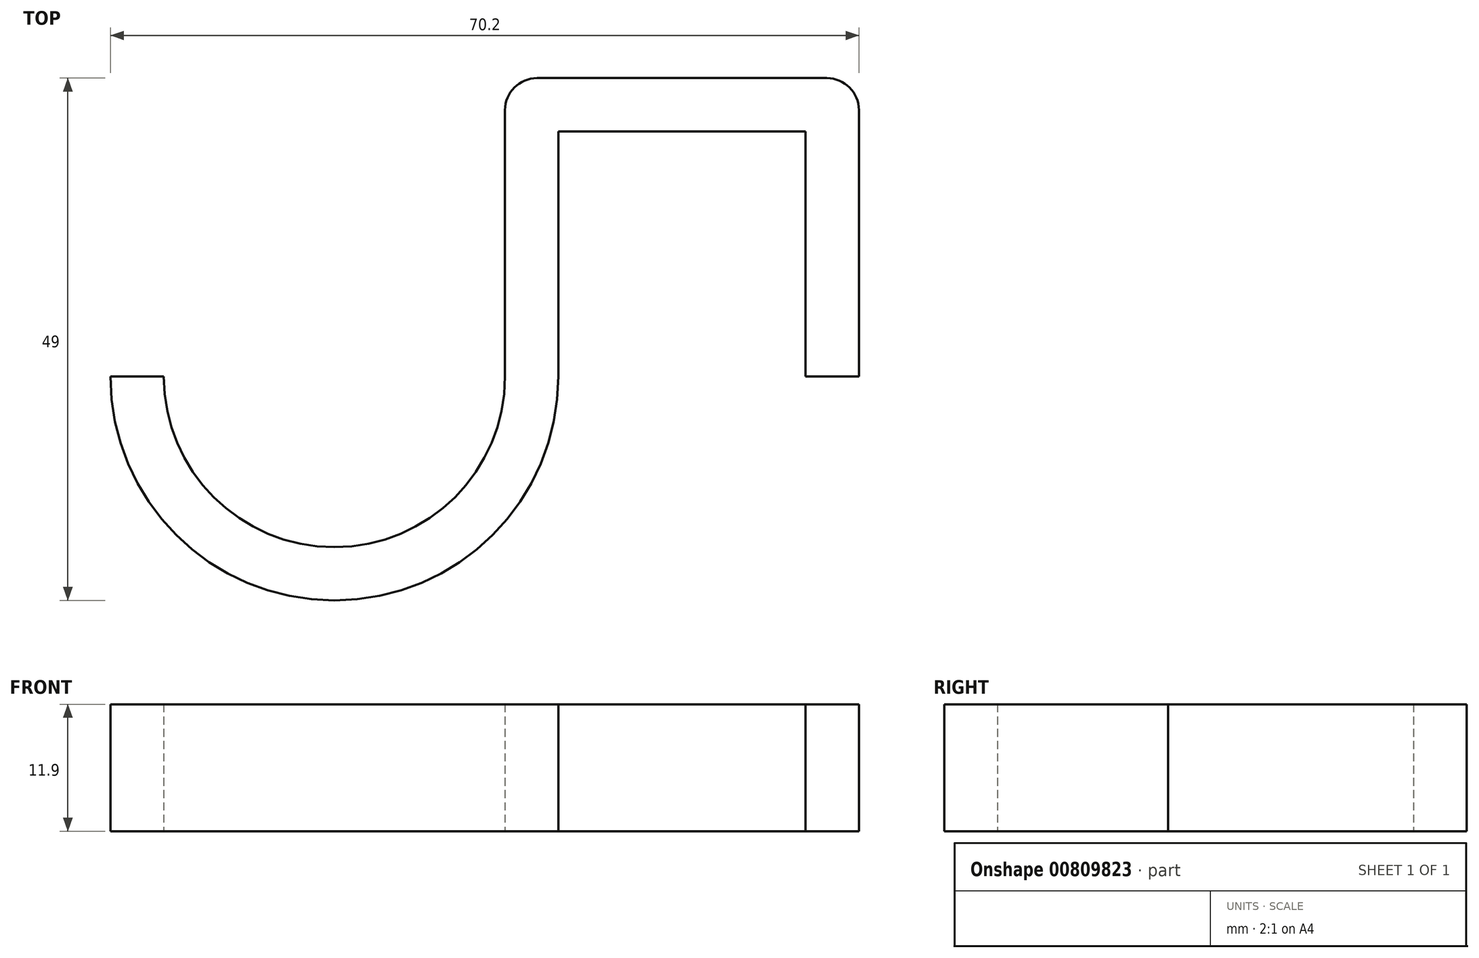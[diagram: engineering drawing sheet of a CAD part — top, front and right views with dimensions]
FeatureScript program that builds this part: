
annotation { "Feature Type Name" : "Feature", "Feature Type Description" : "" }
export const myFeature = defineFeature(function(context is Context, id is Id, definition is map)
    precondition{}
    {
        {
            var Q0;
            Q0=qCreatedBy(makeId("Top.planeOp"),FACE);
            var sketch = newSketch(context, id + "F0", { "sketchPlane" : qUnion([Q0])});
            skLineSegment(sketch, "E0", {"start": v(0, 0) * mm, "end": v(0, 23) * mm});
            skLineSegment(sketch, "E1", {"start": v(0, 23) * mm, "end": v(-23.2, 23) * mm});
            skLineSegment(sketch, "E2", {"start": v(-23.2, 23) * mm, "end": v(-23.2, 0) * mm});
            skArc(sketch, "E3", {"start": v(-65.2, 0) * mm, "mid": v(-44.2, -21) * mm, "end": v(-23.2, 0) * mm});
            skLineSegment(sketch, "E4", {"start": v(5, 0) * mm, "end": v(5, 28) * mm});
            skLineSegment(sketch, "E5", {"start": v(5, 28) * mm, "end": v(-28.2, 28) * mm});
            skLineSegment(sketch, "E6", {"start": v(-28.2, 28) * mm, "end": v(-28.2, 0) * mm});
            skArc(sketch, "E7.0", {"start": v(-60.2, 0) * mm, "mid": v(-44.2, -16) * mm, "end": v(-28.2, 0) * mm});
            skLineSegment(sketch, "E8", {"start": v(-65.2, 0) * mm, "end": v(-60.2, 0) * mm});
            skLineSegment(sketch, "E9", {"start": v(0, 0) * mm, "end": v(5, 0) * mm});
            skSolve(sketch);
        }
        {
            var Q0;
            Q0=makeQuery(id+"F0.imprint","IMPRINT",FACE,{"disambiguationData":[TD([[makeQuery(id+"F0.imprint","IMPRINT",EDGE,{"derivedFrom":sQuery(id+"F0.wireOp",EDGE,"E0")}),-1.0]])]});
            extrude(context, id + "F1", {"entities" : qUnion([Q0]), "depth" : 11.9 * mm, "offsetDistance" : 25 * mm});
        }
        {
            var Q0;
            Q0=makeQuery(id+"F1.opExtrude","SWEPT_EDGE",EDGE,{"disambiguationData":[OSD([sQuery(id+"F0.wireOp",EDGE,"E5"),sQuery(id+"F0.wireOp",EDGE,"E6")])]});
            var Q1;
            Q1=makeQuery(id+"F1.opExtrude","SWEPT_EDGE",EDGE,{"disambiguationData":[OSD([sQuery(id+"F0.wireOp",EDGE,"E4"),sQuery(id+"F0.wireOp",EDGE,"E5")])]});
            fillet(context, id + "F2", {"entities" : qUnion([Q0, Q1]), "radius" : 3 * mm, "tangentPropagation" : true, "allowEdgeOverflow" : false});
        }
    });
